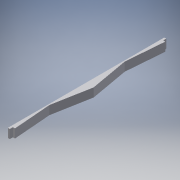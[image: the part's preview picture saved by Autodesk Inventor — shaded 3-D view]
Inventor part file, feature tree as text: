
AUTODESK INVENTOR PART (.ipt)
format: ipt  version: 2017 (Build 210142000, 142)  size: 121,856 bytes
history: native  units: in
note: dims shown in document units (in); Inventor stores cm internally (conversion verified against a paired STEP export)
features: extrude x3, sketch x3
ambient origin geometry x8: Origin, YZ Plane, XZ Plane, XY Plane, X Axis, Y Axis, Z Axis, Center Point
bodies: Solid1 (feature_tree)
feature tree (6):
  extrude  "Extrusion1"  Depth=0.134in
  sketch  "Sketch2"  dims[d2=0.134in d3=1.2285in]
  extrude  "Extrusion2"  Depth=0.134in
  extrude  "Extrusion3"  Depth=1.229in
  sketch  "Sketch1"  dims[d0=4.931in d1=0.134in]
  sketch  "Sketch3"  dims[d4=2.457in d5=1.229in d6=0.2875in d7=0.0in d8=0.065in d9=0.065in d10=0.101in d11=0.0in d12=0.101in d13=0.0in d15=0.259in d16=0.035in d17=0.035in]
